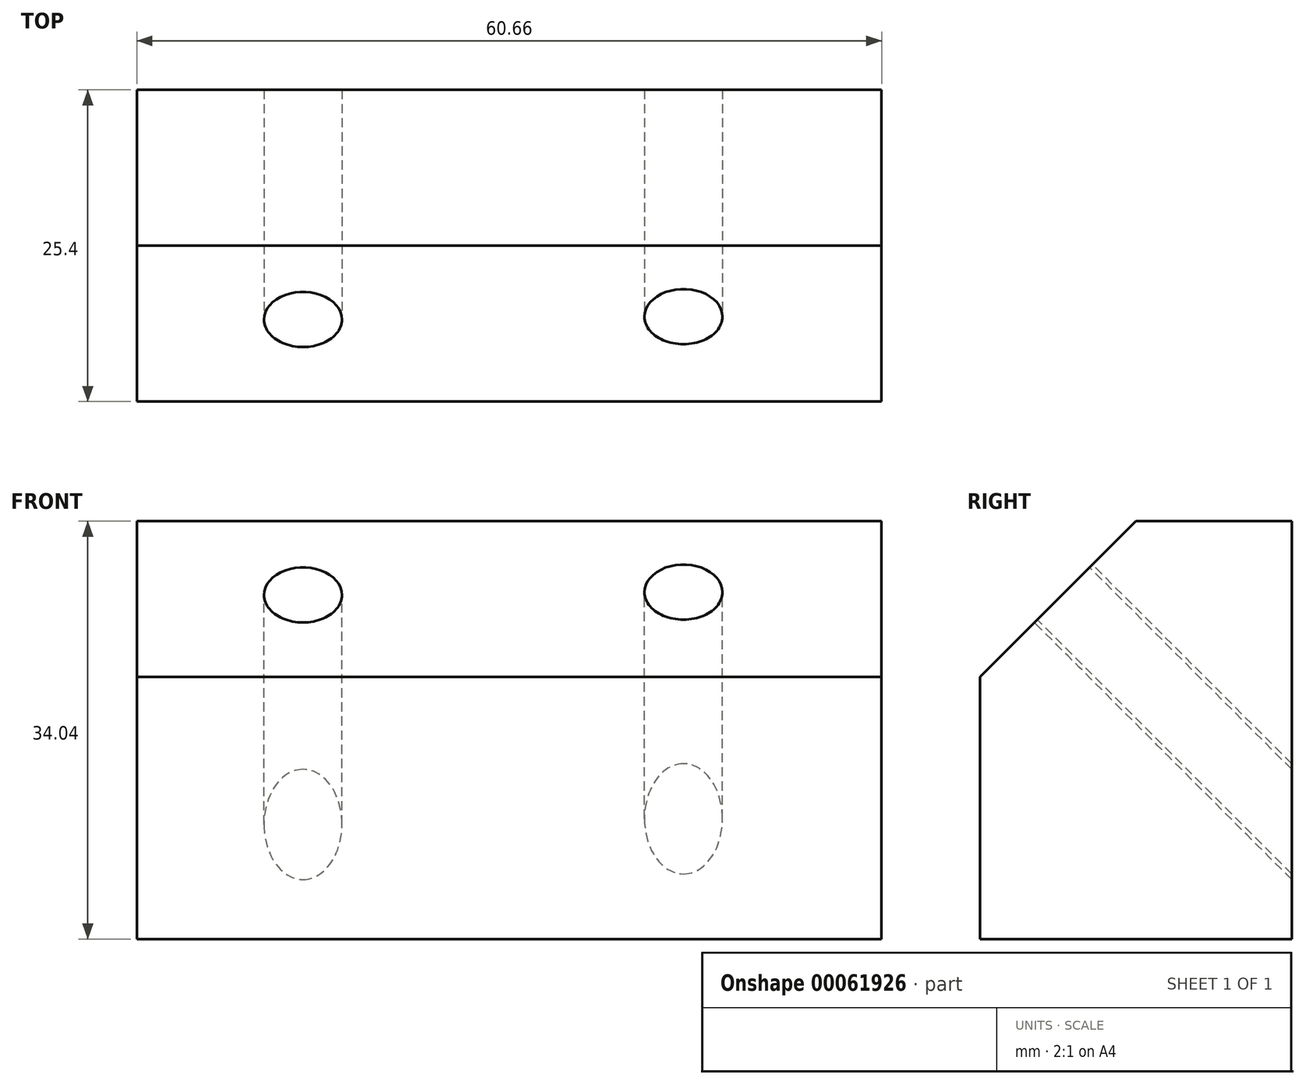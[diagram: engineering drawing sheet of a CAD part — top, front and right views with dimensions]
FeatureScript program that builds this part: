
annotation { "Feature Type Name" : "Feature", "Feature Type Description" : "" }
export const myFeature = defineFeature(function(context is Context, id is Id, definition is map)
    precondition{}
    {
        {
            var Q0;
            Q0=qCreatedBy(makeId("Front.planeOp"),FACE);
            var sketch = newSketch(context, id + "F0", { "sketchPlane" : qUnion([Q0])});
            skLineSegment(sketch, "E0.bottom", {"start": v(-26.77, 19.03) * mm, "end": v(33.89, 19.03) * mm});
            skLineSegment(sketch, "E0.top", {"start": v(-26.77, -15) * mm, "end": v(33.89, -15) * mm});
            skLineSegment(sketch, "E0.left", {"start": v(-26.77, 19.03) * mm, "end": v(-26.77, -15) * mm});
            skLineSegment(sketch, "E0.right", {"start": v(33.89, 19.03) * mm, "end": v(33.89, -15) * mm});
            skSolve(sketch);
        }
        {
            var Q0;
            Q0 = qSketchRegion(id + "F0", true);
            extrude(context, id + "F1", {"entities" : qUnion([Q0]), "depth" : 25.4 * mm});
        }
        {
            var Q0;
            Q0=makeQuery(id+"F1.opExtrude","CAP_EDGE",EDGE,{"disambiguationData":[OSD([sQuery(id+"F0.wireOp",EDGE,"E0.bottom")])],"isStart":false});
            chamfer(context, id + "F2", {"entities" : qUnion([Q0]), "width" : 12.7 * mm, "tangentPropagation" : true});
        }
        {
            var Q0;
            Q0=makeQuery(id+"F2.opChamfer","BLEND_FACE",FACE,{"disambiguationData":[OSD([sQuery(id+"F0.wireOp",EDGE,"E0.bottom")])]});
            var sketch = newSketch(context, id + "F3", { "sketchPlane" : qUnion([Q0])});
            skPoint(sketch, "E1", {"position": v(-13.24, -4.01) * mm});
            skPoint(sketch, "E2", {"position": v(17.75, -3.69) * mm});
            skSolve(sketch);
        }
        {
            var Q0;
            Q0=sQuery(id+"F3.wireOp",VERTEX,"E1");
            var Q1;
            Q1=sQuery(id+"F3.wireOp",VERTEX,"E2");
            var Q2;
            Q2=makeQuery(id+"F1.opExtrude","SWEPT_BODY",BODY,{"disambiguationData":[OSD([sQuery(id+"F0.wireOp",EDGE,"E0.bottom"),sQuery(id+"F0.wireOp",EDGE,"E0.top"),sQuery(id+"F0.wireOp",EDGE,"E0.left"),sQuery(id+"F0.wireOp",EDGE,"E0.right")])]});
            hole(context, id + "F4", {"style" : HoleStyle.SIMPLE, "holeDiameter" : 6.35 * mm, "endStyle" : HoleEndStyle.THROUGH, "locations" : qUnion([Q0, Q1]), "scope" : qUnion([Q2])});
        }
    });
